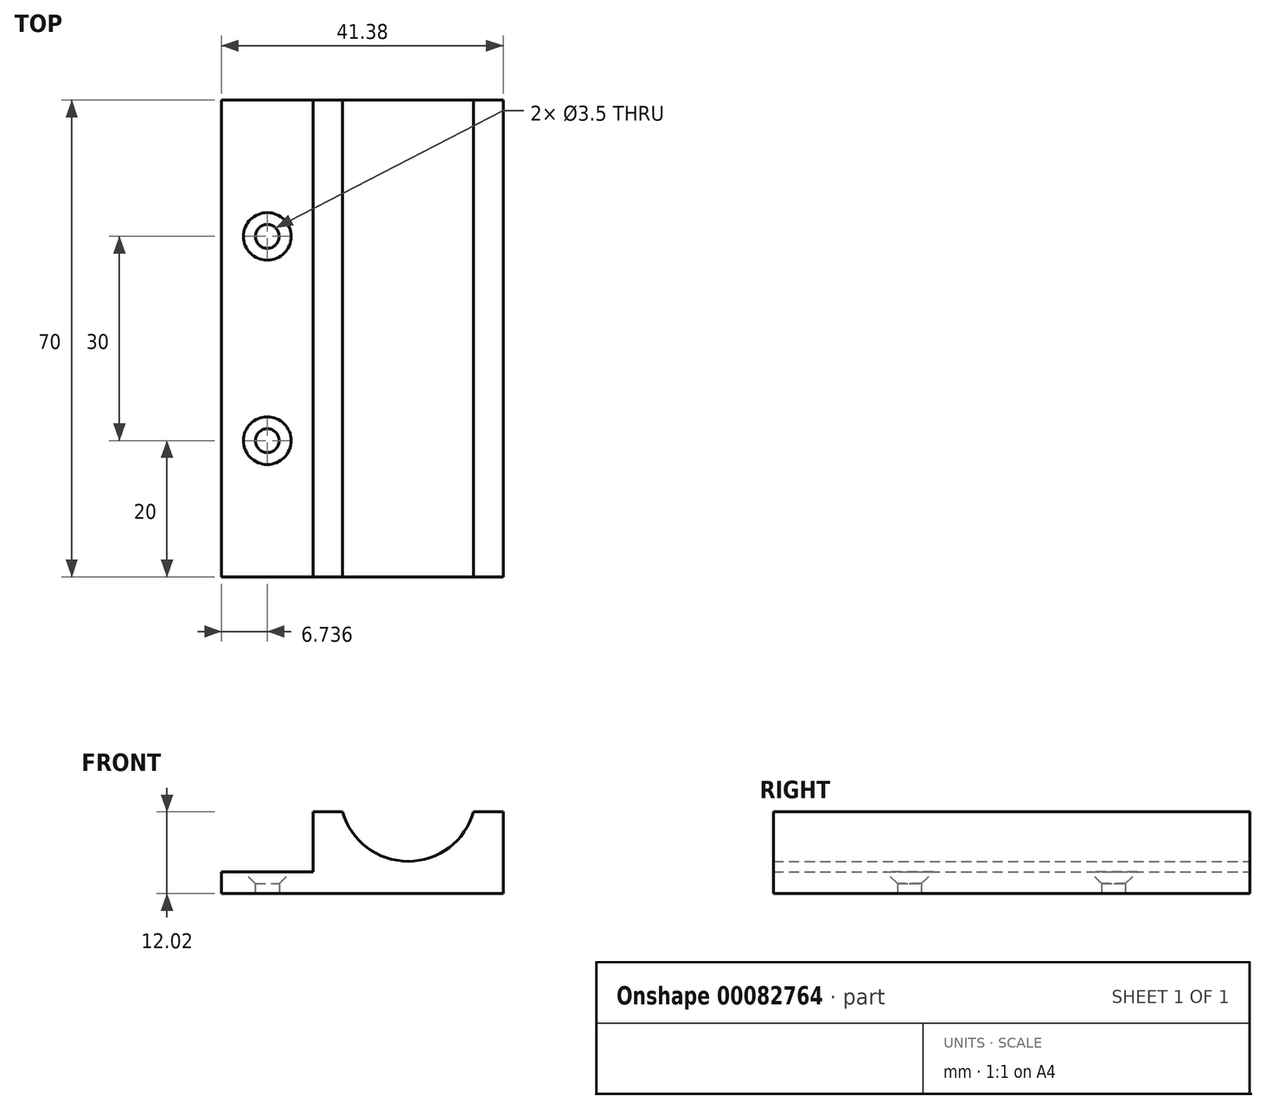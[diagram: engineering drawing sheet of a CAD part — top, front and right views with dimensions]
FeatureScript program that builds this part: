
annotation { "Feature Type Name" : "Feature", "Feature Type Description" : "" }
export const myFeature = defineFeature(function(context is Context, id is Id, definition is map)
    precondition{}
    {
        {
            assignVariable(context, id + "F0", {"name" : "BoltDiameter", "anyValue" : 3.5});
        }
        {
            var Q0;
            Q0=qCreatedBy(makeId("Front.planeOp"),FACE);
            var sketch = newSketch(context, id + "F1", { "sketchPlane" : qUnion([Q0])});
            skLineSegment(sketch, "E0", {"start": v(0, 0) * mm, "end": v(41.38, 0) * mm});
            skLineSegment(sketch, "E1", {"start": v(41.38, 0) * mm, "end": v(41.38, 12.02) * mm});
            skLineSegment(sketch, "E2", {"start": v(41.38, 12.02) * mm, "end": v(13.47, 12.02) * mm});
            skLineSegment(sketch, "E3", {"start": v(13.47, 12.02) * mm, "end": v(13.47, 3.22) * mm});
            skLineSegment(sketch, "E4", {"start": v(13.47, 3.22) * mm, "end": v(0, 3.22) * mm});
            skLineSegment(sketch, "E5", {"start": v(0, 3.22) * mm, "end": v(0, 0) * mm});
            skCircle(sketch, "E6", {"center": v(27.43, 14.75) * mm, "radius": 10 * mm});
            skPoint(sketch, "E6.centerSnap0", {"position": v(27.43, 12.02) * mm});
            skSolve(sketch);
        }
        {
            var Q0;
            Q0=makeQuery(id+"F1.imprint","IMPRINT",FACE,{"disambiguationData":[TD([[makeQuery(id+"F1.imprint","IMPRINT",EDGE,{"derivedFrom":sQuery(id+"F1.wireOp",EDGE,"E0")}),1.0]])]});
            extrude(context, id + "F2", {"entities" : qUnion([Q0]), "depth" : 70 * mm});
        }
        {
            var Q0;
            Q0=makeQuery(id+"F2.opExtrude","SWEPT_FACE",FACE,{"disambiguationData":[OSD([sQuery(id+"F1.wireOp",EDGE,"E4")])]});
            var sketch = newSketch(context, id + "F3", { "sketchPlane" : qUnion([Q0])});
            skLineSegment(sketch, "E7.0", {"start": v(13.47, 0) * mm, "end": v(0, 0) * mm, "construction": true});
            skLineSegment(sketch, "E7.1", {"start": v(0, -70) * mm, "end": v(0, 0) * mm, "construction": true});
            skLineSegment(sketch, "E7.2", {"start": v(13.47, -70) * mm, "end": v(13.47, 0) * mm, "construction": true});
            skLineSegment(sketch, "E7.3", {"start": v(13.47, -70) * mm, "end": v(0, -70) * mm, "construction": true});
            skPoint(sketch, "E8.centerSnap0", {"position": v(6.74, 0) * mm});
            skLineSegment(sketch, "E9", {"start": v(13.47, -35) * mm, "end": v(0, -35) * mm, "construction": true});
            skPoint(sketch, "E10", {"position": v(6.74, -20) * mm});
            skPoint(sketch, "E11.MirrorP", {"position": v(6.74, -50) * mm});
            skSolve(sketch);
        }
        {
            var Q0;
            Q0=sQuery(id+"F3.wireOp",VERTEX,"E10");
            var Q1;
            Q1=sQuery(id+"F3.wireOp",VERTEX,"E11.MirrorP");
            var Q2;
            Q2=makeQuery(id+"F2.opExtrude","SWEPT_BODY",BODY,{"disambiguationData":[OSD([sQuery(id+"F1.wireOp",EDGE,"E0"),sQuery(id+"F1.wireOp",EDGE,"E1"),sQuery(id+"F1.wireOp",EDGE,"E2"),sQuery(id+"F1.wireOp",EDGE,"E3"),sQuery(id+"F1.wireOp",EDGE,"E4"),sQuery(id+"F1.wireOp",EDGE,"E5"),sQuery(id+"F1.wireOp",EDGE,"E6")])]});
            hole(context, id + "F4", {"style" : HoleStyle.C_SINK, "endStyle" : HoleEndStyle.THROUGH, "holeDiameter" : (getVariable(context, 'BoltDiameter')) * mm, "cSinkDiameter" : (getVariable(context, 'BoltDiameter') * 2) * mm, "cSinkAngle" : 90 * degree, "locations" : qUnion([Q0, Q1]), "scope" : qUnion([Q2]), "isTappedThrough" : true});
        }
    });
